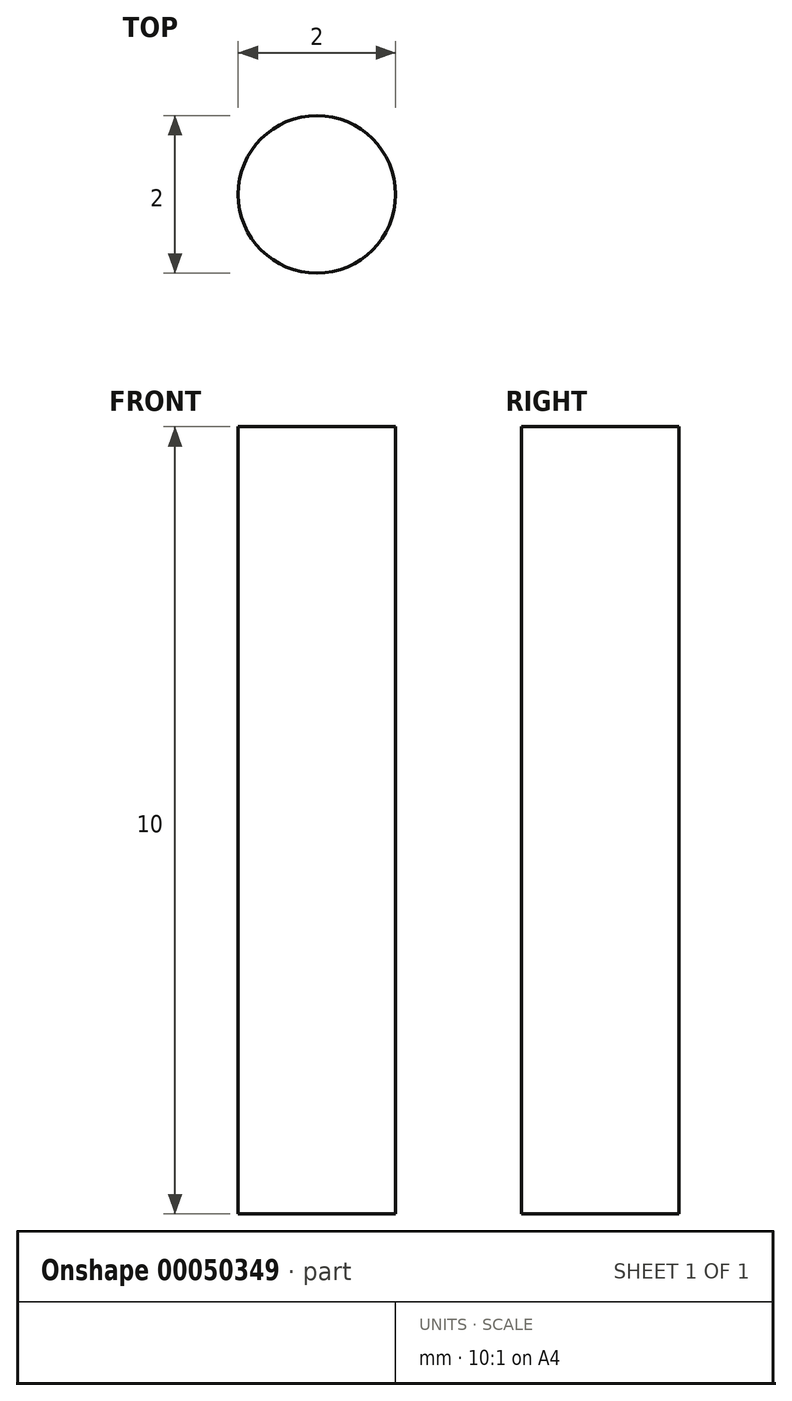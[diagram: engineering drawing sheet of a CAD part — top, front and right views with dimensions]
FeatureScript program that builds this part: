
annotation { "Feature Type Name" : "Feature", "Feature Type Description" : "" }
export const myFeature = defineFeature(function(context is Context, id is Id, definition is map)
    precondition{}
    {
        {
            var Q0;
            Q0=qCreatedBy(makeId("Top.planeOp"),FACE);
            var sketch = newSketch(context, id + "F0", { "sketchPlane" : qUnion([Q0])});
            skCircle(sketch, "E0", {"center": v(0, 0) * mm, "radius": 1 * mm});
            skSolve(sketch);
        }
        {
            var Q0;
            Q0=makeQuery(id+"F0.imprint","IMPRINT",FACE,{"disambiguationData":[TD([[makeQuery(id+"F0.imprint","IMPRINT",EDGE,{"derivedFrom":sQuery(id+"F0.wireOp",EDGE,"E0")}),1.0]])]});
            extrude(context, id + "F1", {"entities" : qUnion([Q0]), "depth" : 10 * mm});
        }
    });
